# Revit family: Pressure independent control valve 4206_R_SMART
name_source: partatom
category: Rohrzubehör
revit_build: Autodesk Revit 2018 (Build: 20190510_1515(x64)
units: mm (PartAtom-declared; Revit-internal decimal feet)

## family parameters
Arbeitsebenenbasiert = Nein
Beim Laden mit Abzugskörper schneiden = Nein
Bemaßung runder Anschluss = Durchmesser verwenden
Gemeinsam genutzt = Nein
Immer vertikal = Ja
OmniClass-Nummer = 23.65.55.14
OmniClass-Titel = Valves for Liquid Services
Teiletyp = Unterbricht

## types (1)
- Pressure independent control valve 4206_R_SMART
    Application = the Pressure Independent Balancing Control Valve (PIBCV) is used in all heating and cooling systems with circulation pumps.
the valve automatically maintains flow to the required part of the system at the set rate by measuring and immediately adjusting to any variation in pressure.
no additional measurements are necessary and the correct flow rate is achieved at all operating conditions.
the diaphragm responds to the pressure upstream and downstream of the regulating valve (via an internal impulse line).
the valve settings directly affect the volumetric flow through the valve.
it is thus possible to set the maximum flow rate based on the flow chart when the valve is fitted.
this allows for the balancing of heating circuits, cooling water systems, ceiling cooling and heating panels, air heaters, etc. without any need to first assess the pressure variations in the system.
the valve‘s principal application is as a control valve for terminal units.
    B01 = 41.62 mm  [stored 0.136549 ft]
    B03 = 7.93 mm  [stored 0.0260171 ft]
    B04 = 6.75 mm  [stored 0.0221457 ft]
    B05 = 3.7 mm  [stored 0.0121391 ft]
    B06 = 5.86 mm  [stored 0.0192257 ft]
    B08 = 23.05 mm  [stored 0.0756234 ft]
    B10 = 31.75 mm
    B11 = 34.69 mm
    B12 = 36.73 mm
    B13 = 40.79 mm  [stored 0.133825 ft]
    B14 = 8.73 mm  [stored 0.0286417 ft]
    B15 = 23 mm  [stored 0.0754593 ft]
    B16 = 26 mm
    Capillary pipe = copper Cu-DHP (CW024A)
    H03 = 3.46 mm  [stored 0.0113517 ft]
    H04 = 6.74 mm  [stored 0.0221129 ft]
    H05 = 10.06 mm  [stored 0.0330052 ft]
    H06 = 24.02 mm  [stored 0.0788058 ft]
    H07 = 28.19 mm  [stored 0.0924869 ft]
    H08 = 4.24 mm  [stored 0.0139108 ft]
    H09 = 1.08 mm
    H10 = 22.33 mm  [stored 0.0732612 ft]
    H11 = 27.6 mm  [stored 0.0905512 ft]
    Hersteller = Herz-Armaturen GmbH
    House = DZR brass CC770S
    L01 = 41 mm  [stored 0.134514 ft]
    L02 = 34 mm
    L05 = 3.44 mm  [stored 0.0112861 ft]
    L06 = 3.44 mm  [stored 0.0112861 ft]
    L07 = 119.30°
    L13 = 32.23 mm  [stored 0.105741 ft]
    L14 = 44 mm  [stored 0.144357 ft]
    Lift = 4 mm  [stored 0.0131234 ft]
    Medium = water purity in accordance with the ÖNORM H5195 and VDI2035 standards
the use of ethylene and propylene glycol in a mixture ratio of 25 - 50% by volume [%] is permitted.
    Membrane = EPDM
    Membrane housing = brass CW602N
    O-Rings = EPDM
    PN = 25
    Pin = stainless steel 14301
    Protective cap = plastic
    SCRNCODE = 05;04;02
    SCRNSEQ = ARM;ARM_TYP="DURR";2
    Spring = spring steel
    URL = http://www.herzvalves.com
    max. Operating pressure = 1600000.0 Pa
    max. Operating temperature from DN40 = 110 °C
    max. Operating temperature up to DN32 = 130 °C
    min. Operating temperature (frost protection) = -20 °C
    min. Operating temperature (pure water) = 2 °C

note: [stored X ft] marks values corroborated as IEEE doubles in the binary element streams (Revit-internal decimal feet)
